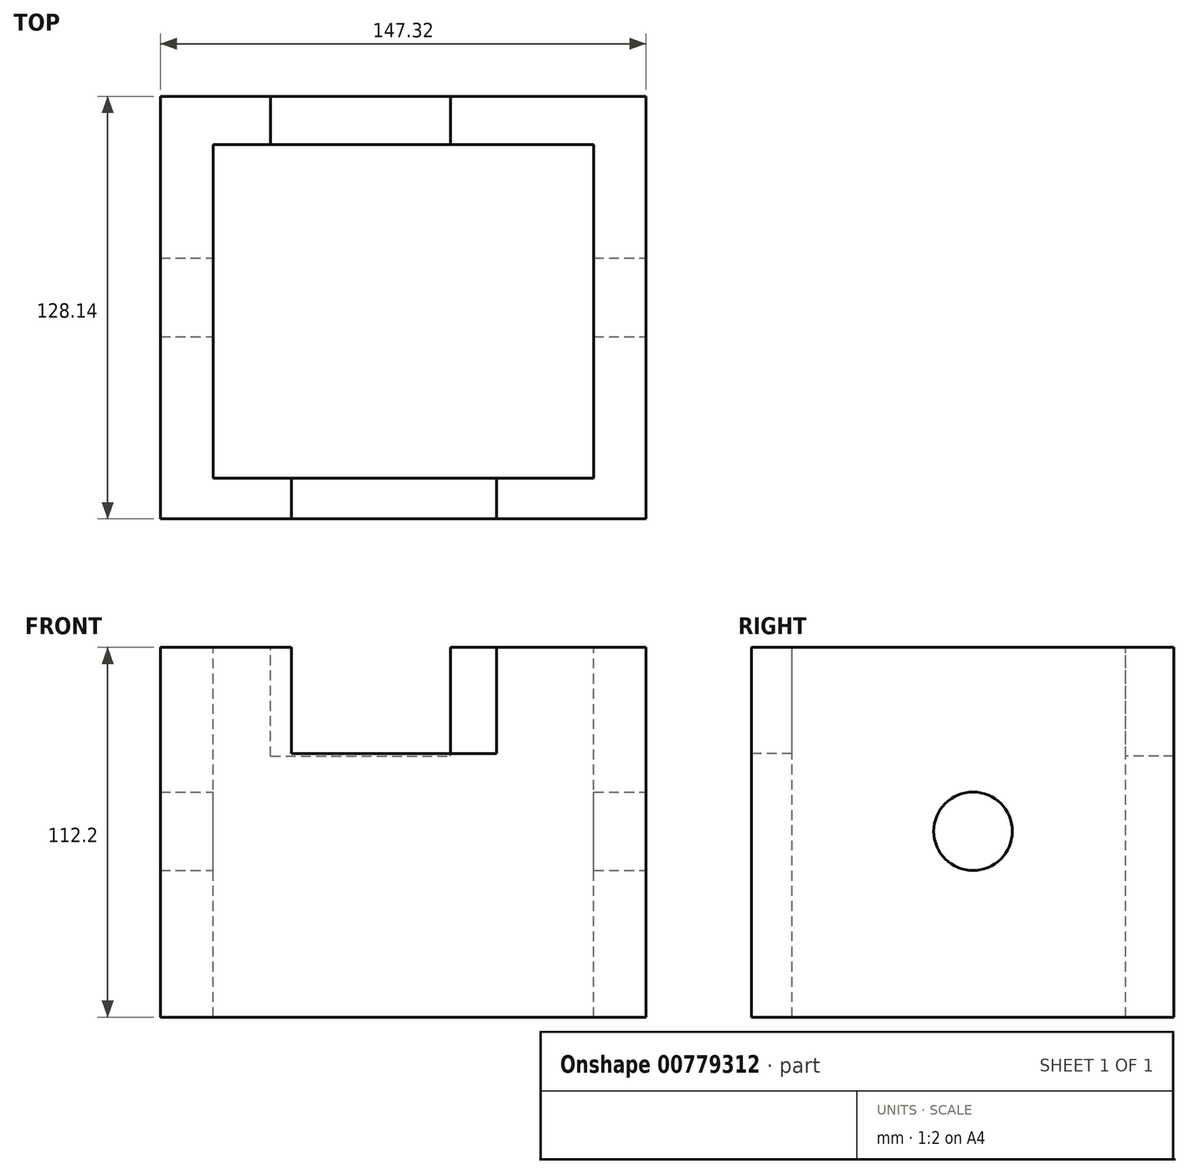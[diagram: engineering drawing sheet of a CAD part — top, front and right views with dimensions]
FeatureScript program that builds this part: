
annotation { "Feature Type Name" : "Feature", "Feature Type Description" : "" }
export const myFeature = defineFeature(function(context is Context, id is Id, definition is map)
    precondition{}
    {
        {
            var Q0;
            Q0=qCreatedBy(makeId("Right.planeOp"),FACE);
            var sketch = newSketch(context, id + "F0", { "sketchPlane" : qUnion([Q0])});
            skLineSegment(sketch, "E0.bottom", {"start": v(-67.23, 55.8) * mm, "end": v(60.9, 55.8) * mm});
            skLineSegment(sketch, "E0.top", {"start": v(-67.23, -56.4) * mm, "end": v(60.9, -56.4) * mm});
            skLineSegment(sketch, "E0.left", {"start": v(-67.23, 55.8) * mm, "end": v(-67.23, -56.4) * mm});
            skLineSegment(sketch, "E0.right", {"start": v(60.9, 55.8) * mm, "end": v(60.9, -56.4) * mm});
            skCircle(sketch, "E1", {"center": v(0, 0) * mm, "radius": 11.92 * mm});
            skSolve(sketch);
        }
        {
            var Q0;
            Q0=makeQuery(id+"F0.imprint","IMPRINT",FACE,{"disambiguationData":[TD([[makeQuery(id+"F0.imprint","IMPRINT",EDGE,{"derivedFrom":sQuery(id+"F0.wireOp",EDGE,"E0.bottom")}),-1.0]])]});
            extrude(context, id + "F1", {"entities" : qUnion([Q0]), "oppositeDirection" : true, "depth" : 147.32 * mm, "offsetDistance" : 25.4 * mm});
        }
        {
            var Q0;
            Q0=makeQuery(id+"F1.opExtrude","SWEPT_FACE",FACE,{"disambiguationData":[OSD([sQuery(id+"F0.wireOp",EDGE,"E0.bottom")])]});
            var sketch = newSketch(context, id + "F2", { "sketchPlane" : qUnion([Q0])});
            skLineSegment(sketch, "E2.bottom", {"start": v(-131.26, -54.95) * mm, "end": v(-15.82, -54.95) * mm});
            skLineSegment(sketch, "E2.top", {"start": v(-131.26, 46.37) * mm, "end": v(-15.82, 46.37) * mm});
            skLineSegment(sketch, "E2.left", {"start": v(-131.26, -54.95) * mm, "end": v(-131.26, 46.37) * mm});
            skLineSegment(sketch, "E2.right", {"start": v(-15.82, -54.95) * mm, "end": v(-15.82, 46.37) * mm});
            skSolve(sketch);
        }
        {
            var Q0;
            Q0=makeQuery(id+"F2.imprint","IMPRINT",FACE,{"disambiguationData":[TD([[makeQuery(id+"F2.imprint","IMPRINT",EDGE,{"derivedFrom":sQuery(id+"F2.wireOp",EDGE,"E2.bottom")}),1.0]])]});
            extrude(context, id + "F3", {"entities" : qUnion([Q0]), "operationType" : NewBodyOperationType.REMOVE, "endBound" : BoundingType.THROUGH_ALL, "oppositeDirection" : true, "depth" : 25.4 * mm, "offsetDistance" : 25.4 * mm});
        }
        {
            var Q0;
            Q0=makeQuery(id+"F1.opExtrude","SWEPT_FACE",FACE,{"disambiguationData":[OSD([sQuery(id+"F0.wireOp",EDGE,"E0.bottom")])]});
            var sketch = newSketch(context, id + "F4", { "sketchPlane" : qUnion([Q0])});
            skLineSegment(sketch, "E3.bottom", {"start": v(-107.53, -54.95) * mm, "end": v(-45.33, -54.95) * mm});
            skLineSegment(sketch, "E3.top", {"start": v(-107.53, -67.23) * mm, "end": v(-45.33, -67.23) * mm});
            skLineSegment(sketch, "E3.left", {"start": v(-107.53, -54.95) * mm, "end": v(-107.53, -67.23) * mm});
            skLineSegment(sketch, "E3.right", {"start": v(-45.33, -54.95) * mm, "end": v(-45.33, -67.23) * mm});
            skLineSegment(sketch, "E4.bottom", {"start": v(-113.87, 60.9) * mm, "end": v(-59.32, 60.9) * mm});
            skLineSegment(sketch, "E4.top", {"start": v(-113.87, 46.37) * mm, "end": v(-59.32, 46.37) * mm});
            skLineSegment(sketch, "E4.left", {"start": v(-113.87, 60.9) * mm, "end": v(-113.87, 46.37) * mm});
            skLineSegment(sketch, "E4.right", {"start": v(-59.32, 60.9) * mm, "end": v(-59.32, 46.37) * mm});
            skSolve(sketch);
        }
        {
            var Q0;
            Q0=makeQuery(id+"F4.imprint","IMPRINT",FACE,{"disambiguationData":[TD([[makeQuery(id+"F4.imprint","IMPRINT",EDGE,{"derivedFrom":sQuery(id+"F4.wireOp",EDGE,"E3.bottom")}),-1.0]])]});
            extrude(context, id + "F5", {"entities" : qUnion([Q0]), "operationType" : NewBodyOperationType.REMOVE, "oppositeDirection" : true, "depth" : 32.26 * mm, "offsetDistance" : 25.4 * mm});
        }
        {
            var Q0;
            Q0=makeQuery(id+"F4.imprint","IMPRINT",FACE,{"disambiguationData":[TD([[makeQuery(id+"F4.imprint","IMPRINT",EDGE,{"derivedFrom":sQuery(id+"F4.wireOp",EDGE,"E4.bottom")}),-1.0]])]});
            extrude(context, id + "F6", {"entities" : qUnion([Q0]), "operationType" : NewBodyOperationType.REMOVE, "oppositeDirection" : true, "depth" : 33.02 * mm, "offsetDistance" : 25.4 * mm});
        }
    });
